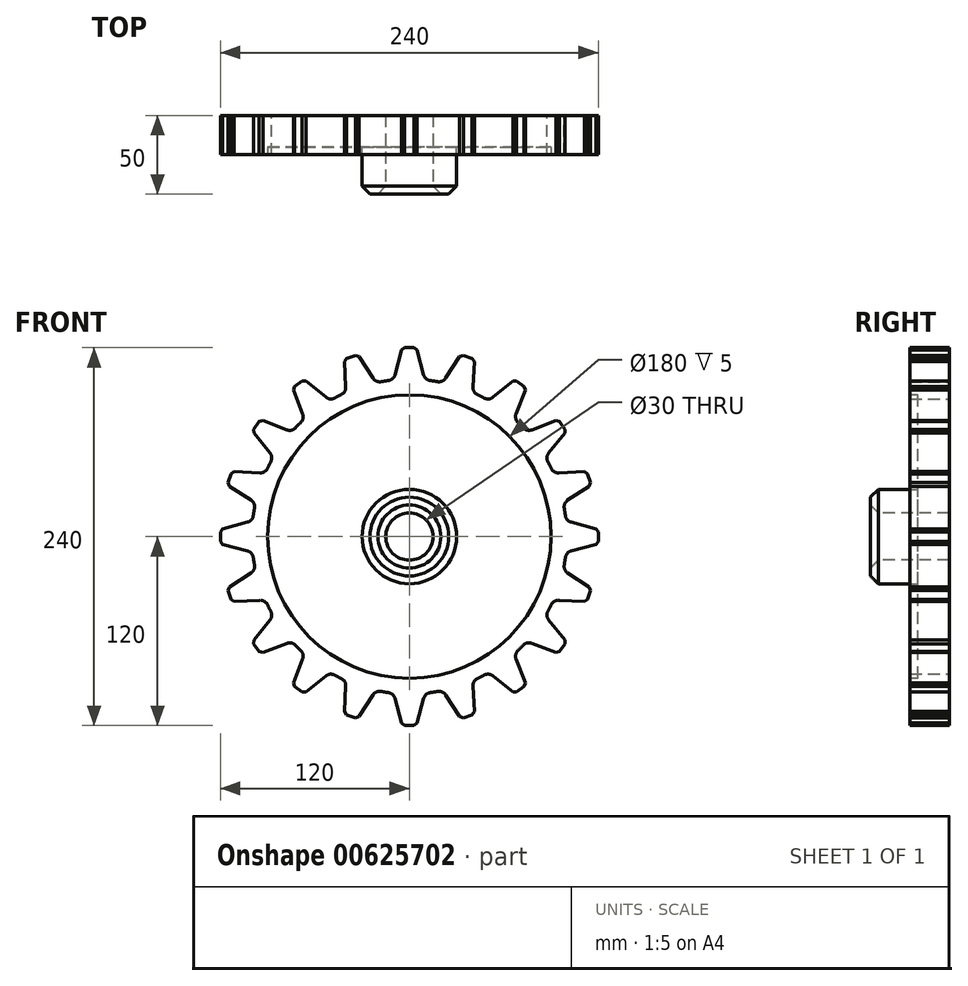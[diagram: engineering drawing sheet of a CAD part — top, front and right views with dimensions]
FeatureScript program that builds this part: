
annotation { "Feature Type Name" : "Feature", "Feature Type Description" : "" }
export const myFeature = defineFeature(function(context is Context, id is Id, definition is map)
    precondition{}
    {
        {
            var Q0;
            Q0=qCreatedBy(makeId("Front.planeOp"),FACE);
            var sketch = newSketch(context, id + "F0", { "sketchPlane" : qUnion([Q0])});
            skArc(sketch, "E0", {"start": v(21.24, 97.72) * mm, "mid": v(15.64, 98.77) * mm, "end": v(10, 99.5) * mm});
            skCircle(sketch, "E1", {"center": v(0, 0) * mm, "radius": 120 * mm, "construction": true});
            skLineSegment(sketch, "E2", {"start": v(0, 120) * mm, "end": v(-4.5, 120) * mm});
            skLineSegment(sketch, "E3", {"start": v(0, 120) * mm, "end": v(4.5, 120) * mm});
            skLineSegment(sketch, "E4", {"start": v(-4.5, 120) * mm, "end": v(-10, 99.5) * mm});
            skLineSegment(sketch, "E5", {"start": v(4.5, 120) * mm, "end": v(10, 99.5) * mm});
            skLineSegment(sketch, "E6.1.0", {"start": v(-41.36, 112.74) * mm, "end": v(-40.25, 91.54) * mm});
            skLineSegment(sketch, "E6.1.1", {"start": v(-37.08, 114.13) * mm, "end": v(-41.36, 112.74) * mm});
            skLineSegment(sketch, "E6.1.2", {"start": v(-37.08, 114.13) * mm, "end": v(-32.8, 115.52) * mm});
            skLineSegment(sketch, "E6.1.3", {"start": v(-32.8, 115.52) * mm, "end": v(-21.24, 97.72) * mm});
            skLineSegment(sketch, "E6.2.0", {"start": v(-74.17, 94.44) * mm, "end": v(-66.57, 74.62) * mm});
            skLineSegment(sketch, "E6.2.1", {"start": v(-70.53, 97.08) * mm, "end": v(-74.17, 94.44) * mm});
            skLineSegment(sketch, "E6.2.2", {"start": v(-70.53, 97.08) * mm, "end": v(-66.9, 99.73) * mm});
            skLineSegment(sketch, "E6.2.3", {"start": v(-66.9, 99.73) * mm, "end": v(-50.4, 86.37) * mm});
            skLineSegment(sketch, "E6.3.0", {"start": v(-99.73, 66.9) * mm, "end": v(-86.37, 50.4) * mm});
            skLineSegment(sketch, "E6.3.1", {"start": v(-97.08, 70.53) * mm, "end": v(-99.73, 66.9) * mm});
            skLineSegment(sketch, "E6.3.2", {"start": v(-97.08, 70.53) * mm, "end": v(-94.44, 74.17) * mm});
            skLineSegment(sketch, "E6.3.3", {"start": v(-94.44, 74.17) * mm, "end": v(-74.62, 66.57) * mm});
            skLineSegment(sketch, "E6.4.0", {"start": v(-115.52, 32.8) * mm, "end": v(-97.72, 21.24) * mm});
            skLineSegment(sketch, "E6.4.1", {"start": v(-114.13, 37.08) * mm, "end": v(-115.52, 32.8) * mm});
            skLineSegment(sketch, "E6.4.2", {"start": v(-114.13, 37.08) * mm, "end": v(-112.74, 41.36) * mm});
            skLineSegment(sketch, "E6.4.3", {"start": v(-112.74, 41.36) * mm, "end": v(-91.54, 40.25) * mm});
            skLineSegment(sketch, "E6.5.0", {"start": v(-120, -4.5) * mm, "end": v(-99.5, -10) * mm});
            skLineSegment(sketch, "E6.5.1", {"start": v(-120, 0) * mm, "end": v(-120, -4.5) * mm});
            skLineSegment(sketch, "E6.5.2", {"start": v(-120, 0) * mm, "end": v(-120, 4.5) * mm});
            skLineSegment(sketch, "E6.5.3", {"start": v(-120, 4.5) * mm, "end": v(-99.5, 10) * mm});
            skLineSegment(sketch, "E6.6.0", {"start": v(-112.74, -41.36) * mm, "end": v(-91.54, -40.25) * mm});
            skLineSegment(sketch, "E6.6.1", {"start": v(-114.13, -37.08) * mm, "end": v(-112.74, -41.36) * mm});
            skLineSegment(sketch, "E6.6.2", {"start": v(-114.13, -37.08) * mm, "end": v(-115.52, -32.8) * mm});
            skLineSegment(sketch, "E6.6.3", {"start": v(-115.52, -32.8) * mm, "end": v(-97.72, -21.24) * mm});
            skLineSegment(sketch, "E6.7.0", {"start": v(-94.44, -74.17) * mm, "end": v(-74.62, -66.57) * mm});
            skLineSegment(sketch, "E6.7.1", {"start": v(-97.08, -70.53) * mm, "end": v(-94.44, -74.17) * mm});
            skLineSegment(sketch, "E6.7.2", {"start": v(-97.08, -70.53) * mm, "end": v(-99.73, -66.9) * mm});
            skLineSegment(sketch, "E6.7.3", {"start": v(-99.73, -66.9) * mm, "end": v(-86.37, -50.4) * mm});
            skLineSegment(sketch, "E6.8.0", {"start": v(-66.9, -99.73) * mm, "end": v(-50.4, -86.37) * mm});
            skLineSegment(sketch, "E6.8.1", {"start": v(-70.53, -97.08) * mm, "end": v(-66.9, -99.73) * mm});
            skLineSegment(sketch, "E6.8.2", {"start": v(-70.53, -97.08) * mm, "end": v(-74.17, -94.44) * mm});
            skLineSegment(sketch, "E6.8.3", {"start": v(-74.17, -94.44) * mm, "end": v(-66.57, -74.62) * mm});
            skLineSegment(sketch, "E6.9.0", {"start": v(-32.8, -115.52) * mm, "end": v(-21.24, -97.72) * mm});
            skLineSegment(sketch, "E6.9.1", {"start": v(-37.08, -114.13) * mm, "end": v(-32.8, -115.52) * mm});
            skLineSegment(sketch, "E6.9.2", {"start": v(-37.08, -114.13) * mm, "end": v(-41.36, -112.74) * mm});
            skLineSegment(sketch, "E6.9.3", {"start": v(-41.36, -112.74) * mm, "end": v(-40.25, -91.54) * mm});
            skLineSegment(sketch, "E6.10.0", {"start": v(4.5, -120) * mm, "end": v(10, -99.5) * mm});
            skLineSegment(sketch, "E6.10.1", {"start": v(0, -120) * mm, "end": v(4.5, -120) * mm});
            skLineSegment(sketch, "E6.10.2", {"start": v(0, -120) * mm, "end": v(-4.5, -120) * mm});
            skLineSegment(sketch, "E6.10.3", {"start": v(-4.5, -120) * mm, "end": v(-10, -99.5) * mm});
            skLineSegment(sketch, "E6.11.0", {"start": v(41.36, -112.74) * mm, "end": v(40.25, -91.54) * mm});
            skLineSegment(sketch, "E6.11.1", {"start": v(37.08, -114.13) * mm, "end": v(41.36, -112.74) * mm});
            skLineSegment(sketch, "E6.11.2", {"start": v(37.08, -114.13) * mm, "end": v(32.8, -115.52) * mm});
            skLineSegment(sketch, "E6.11.3", {"start": v(32.8, -115.52) * mm, "end": v(21.24, -97.72) * mm});
            skLineSegment(sketch, "E6.12.0", {"start": v(74.17, -94.44) * mm, "end": v(66.57, -74.62) * mm});
            skLineSegment(sketch, "E6.12.1", {"start": v(70.53, -97.08) * mm, "end": v(74.17, -94.44) * mm});
            skLineSegment(sketch, "E6.12.2", {"start": v(70.53, -97.08) * mm, "end": v(66.9, -99.73) * mm});
            skLineSegment(sketch, "E6.12.3", {"start": v(66.9, -99.73) * mm, "end": v(50.4, -86.37) * mm});
            skLineSegment(sketch, "E6.13.0", {"start": v(99.73, -66.9) * mm, "end": v(86.37, -50.4) * mm});
            skLineSegment(sketch, "E6.13.1", {"start": v(97.08, -70.53) * mm, "end": v(99.73, -66.9) * mm});
            skLineSegment(sketch, "E6.13.2", {"start": v(97.08, -70.53) * mm, "end": v(94.44, -74.17) * mm});
            skLineSegment(sketch, "E6.13.3", {"start": v(94.44, -74.17) * mm, "end": v(74.62, -66.57) * mm});
            skLineSegment(sketch, "E6.14.0", {"start": v(115.52, -32.8) * mm, "end": v(97.72, -21.24) * mm});
            skLineSegment(sketch, "E6.14.1", {"start": v(114.13, -37.08) * mm, "end": v(115.52, -32.8) * mm});
            skLineSegment(sketch, "E6.14.2", {"start": v(114.13, -37.08) * mm, "end": v(112.74, -41.36) * mm});
            skLineSegment(sketch, "E6.14.3", {"start": v(112.74, -41.36) * mm, "end": v(91.54, -40.25) * mm});
            skLineSegment(sketch, "E6.15.0", {"start": v(120, 4.5) * mm, "end": v(99.5, 10) * mm});
            skLineSegment(sketch, "E6.15.1", {"start": v(120, 0) * mm, "end": v(120, 4.5) * mm});
            skLineSegment(sketch, "E6.15.2", {"start": v(120, 0) * mm, "end": v(120, -4.5) * mm});
            skLineSegment(sketch, "E6.15.3", {"start": v(120, -4.5) * mm, "end": v(99.5, -10) * mm});
            skLineSegment(sketch, "E6.16.0", {"start": v(112.74, 41.36) * mm, "end": v(91.54, 40.25) * mm});
            skLineSegment(sketch, "E6.16.1", {"start": v(114.13, 37.08) * mm, "end": v(112.74, 41.36) * mm});
            skLineSegment(sketch, "E6.16.2", {"start": v(114.13, 37.08) * mm, "end": v(115.52, 32.8) * mm});
            skLineSegment(sketch, "E6.16.3", {"start": v(115.52, 32.8) * mm, "end": v(97.72, 21.24) * mm});
            skLineSegment(sketch, "E6.17.0", {"start": v(94.44, 74.17) * mm, "end": v(74.62, 66.57) * mm});
            skLineSegment(sketch, "E6.17.1", {"start": v(97.08, 70.53) * mm, "end": v(94.44, 74.17) * mm});
            skLineSegment(sketch, "E6.17.2", {"start": v(97.08, 70.53) * mm, "end": v(99.73, 66.9) * mm});
            skLineSegment(sketch, "E6.17.3", {"start": v(99.73, 66.9) * mm, "end": v(86.37, 50.4) * mm});
            skLineSegment(sketch, "E6.18.0", {"start": v(66.9, 99.73) * mm, "end": v(50.4, 86.37) * mm});
            skLineSegment(sketch, "E6.18.1", {"start": v(70.53, 97.08) * mm, "end": v(66.9, 99.73) * mm});
            skLineSegment(sketch, "E6.18.2", {"start": v(70.53, 97.08) * mm, "end": v(74.17, 94.44) * mm});
            skLineSegment(sketch, "E6.18.3", {"start": v(74.17, 94.44) * mm, "end": v(66.57, 74.62) * mm});
            skLineSegment(sketch, "E6.19.0", {"start": v(32.8, 115.52) * mm, "end": v(21.24, 97.72) * mm});
            skLineSegment(sketch, "E6.19.1", {"start": v(37.08, 114.13) * mm, "end": v(32.8, 115.52) * mm});
            skLineSegment(sketch, "E6.19.2", {"start": v(37.08, 114.13) * mm, "end": v(41.36, 112.74) * mm});
            skLineSegment(sketch, "E6.19.3", {"start": v(41.36, 112.74) * mm, "end": v(40.25, 91.54) * mm});
            skArc(sketch, "E7.trimOffspring", {"start": v(-40.25, 91.54) * mm, "mid": v(-45.4, 89.1) * mm, "end": v(-50.4, 86.37) * mm});
            skArc(sketch, "E8.trimOffspring", {"start": v(-66.57, 74.62) * mm, "mid": v(-70.71, 70.71) * mm, "end": v(-74.62, 66.57) * mm});
            skArc(sketch, "E9.trimOffspring", {"start": v(-86.37, 50.4) * mm, "mid": v(-89.1, 45.4) * mm, "end": v(-91.54, 40.25) * mm});
            skArc(sketch, "E10.trimOffspring", {"start": v(-97.72, 21.24) * mm, "mid": v(-98.77, 15.64) * mm, "end": v(-99.5, 10) * mm});
            skArc(sketch, "E11.trimOffspring", {"start": v(-99.5, -10) * mm, "mid": v(-98.77, -15.64) * mm, "end": v(-97.72, -21.24) * mm});
            skArc(sketch, "E12.trimOffspring", {"start": v(-91.54, -40.25) * mm, "mid": v(-89.1, -45.4) * mm, "end": v(-86.37, -50.4) * mm});
            skArc(sketch, "E13.trimOffspring", {"start": v(-74.62, -66.57) * mm, "mid": v(-70.71, -70.71) * mm, "end": v(-66.57, -74.62) * mm});
            skArc(sketch, "E14.trimOffspring", {"start": v(-50.4, -86.37) * mm, "mid": v(-45.4, -89.1) * mm, "end": v(-40.25, -91.54) * mm});
            skArc(sketch, "E15.trimOffspring", {"start": v(-21.24, -97.72) * mm, "mid": v(-15.64, -98.77) * mm, "end": v(-10, -99.5) * mm});
            skArc(sketch, "E16.trimOffspring", {"start": v(10, -99.5) * mm, "mid": v(15.64, -98.77) * mm, "end": v(21.24, -97.72) * mm});
            skArc(sketch, "E17.trimOffspring", {"start": v(40.25, -91.54) * mm, "mid": v(45.4, -89.1) * mm, "end": v(50.4, -86.37) * mm});
            skArc(sketch, "E18.trimOffspring", {"start": v(66.57, -74.62) * mm, "mid": v(70.71, -70.71) * mm, "end": v(74.62, -66.57) * mm});
            skArc(sketch, "E19.trimOffspring", {"start": v(86.37, -50.4) * mm, "mid": v(89.1, -45.4) * mm, "end": v(91.54, -40.25) * mm});
            skArc(sketch, "E20.trimOffspring", {"start": v(97.72, -21.24) * mm, "mid": v(98.77, -15.64) * mm, "end": v(99.5, -10) * mm});
            skArc(sketch, "E21.trimOffspring", {"start": v(99.5, 10) * mm, "mid": v(98.77, 15.64) * mm, "end": v(97.72, 21.24) * mm});
            skArc(sketch, "E22.trimOffspring", {"start": v(91.54, 40.25) * mm, "mid": v(89.1, 45.4) * mm, "end": v(86.37, 50.4) * mm});
            skArc(sketch, "E23.trimOffspring", {"start": v(74.62, 66.57) * mm, "mid": v(70.71, 70.71) * mm, "end": v(66.57, 74.62) * mm});
            skArc(sketch, "E24.trimOffspring", {"start": v(50.4, 86.37) * mm, "mid": v(45.4, 89.1) * mm, "end": v(40.25, 91.54) * mm});
            skArc(sketch, "E25.trimOffspring", {"start": v(-10, 99.5) * mm, "mid": v(-15.64, 98.77) * mm, "end": v(-21.24, 97.72) * mm});
            skSolve(sketch);
        }
        {
            var Q0;
            Q0=makeQuery(id+"F0.imprint","IMPRINT",FACE,{"disambiguationData":[TD([[makeQuery(id+"F0.imprint","IMPRINT",EDGE,{"derivedFrom":sQuery(id+"F0.wireOp",EDGE,"E0")}),1.0]])]});
            extrude(context, id + "F1", {"entities" : qUnion([Q0]), "depth" : 25 * mm, "offsetDistance" : 25 * mm});
        }
        {
            var Q0;
            Q0=makeQuery(id+"F1.opExtrude","SWEPT_EDGE",EDGE,{"disambiguationData":[OSD([sQuery(id+"F0.wireOp",EDGE,"E0"),sQuery(id+"F0.wireOp",EDGE,"E5")])]});
            var Q1;
            Q1=makeQuery(id+"F1.opExtrude","SWEPT_EDGE",EDGE,{"disambiguationData":[OSD([sQuery(id+"F0.wireOp",EDGE,"E0"),sQuery(id+"F0.wireOp",EDGE,"E6.19.0")])]});
            var Q2;
            Q2=makeQuery(id+"F1.opExtrude","SWEPT_EDGE",EDGE,{"disambiguationData":[OSD([sQuery(id+"F0.wireOp",EDGE,"E6.1.3"),sQuery(id+"F0.wireOp",EDGE,"E25.trimOffspring")])]});
            var Q3;
            Q3=makeQuery(id+"F1.opExtrude","SWEPT_EDGE",EDGE,{"disambiguationData":[OSD([sQuery(id+"F0.wireOp",EDGE,"E4"),sQuery(id+"F0.wireOp",EDGE,"E25.trimOffspring")])]});
            var Q4;
            Q4=makeQuery(id+"F1.opExtrude","SWEPT_EDGE",EDGE,{"disambiguationData":[OSD([sQuery(id+"F0.wireOp",EDGE,"E6.2.3"),sQuery(id+"F0.wireOp",EDGE,"E7.trimOffspring")])]});
            var Q5;
            Q5=makeQuery(id+"F1.opExtrude","SWEPT_EDGE",EDGE,{"disambiguationData":[OSD([sQuery(id+"F0.wireOp",EDGE,"E6.3.3"),sQuery(id+"F0.wireOp",EDGE,"E8.trimOffspring")])]});
            var Q6;
            Q6=makeQuery(id+"F1.opExtrude","SWEPT_EDGE",EDGE,{"disambiguationData":[OSD([sQuery(id+"F0.wireOp",EDGE,"E6.2.0"),sQuery(id+"F0.wireOp",EDGE,"E8.trimOffspring")])]});
            var Q7;
            Q7=makeQuery(id+"F1.opExtrude","SWEPT_EDGE",EDGE,{"disambiguationData":[OSD([sQuery(id+"F0.wireOp",EDGE,"E6.1.0"),sQuery(id+"F0.wireOp",EDGE,"E7.trimOffspring")])]});
            var Q8;
            Q8=makeQuery(id+"F1.opExtrude","SWEPT_EDGE",EDGE,{"disambiguationData":[OSD([sQuery(id+"F0.wireOp",EDGE,"E6.4.3"),sQuery(id+"F0.wireOp",EDGE,"E9.trimOffspring")])]});
            var Q9;
            Q9=makeQuery(id+"F1.opExtrude","SWEPT_EDGE",EDGE,{"disambiguationData":[OSD([sQuery(id+"F0.wireOp",EDGE,"E6.3.0"),sQuery(id+"F0.wireOp",EDGE,"E9.trimOffspring")])]});
            var Q10;
            Q10=makeQuery(id+"F1.opExtrude","SWEPT_EDGE",EDGE,{"disambiguationData":[OSD([sQuery(id+"F0.wireOp",EDGE,"E6.5.3"),sQuery(id+"F0.wireOp",EDGE,"E10.trimOffspring")])]});
            var Q11;
            Q11=makeQuery(id+"F1.opExtrude","SWEPT_EDGE",EDGE,{"disambiguationData":[OSD([sQuery(id+"F0.wireOp",EDGE,"E6.4.0"),sQuery(id+"F0.wireOp",EDGE,"E10.trimOffspring")])]});
            var Q12;
            Q12=makeQuery(id+"F1.opExtrude","SWEPT_EDGE",EDGE,{"disambiguationData":[OSD([sQuery(id+"F0.wireOp",EDGE,"E6.5.0"),sQuery(id+"F0.wireOp",EDGE,"E11.trimOffspring")])]});
            var Q13;
            Q13=makeQuery(id+"F1.opExtrude","SWEPT_EDGE",EDGE,{"disambiguationData":[OSD([sQuery(id+"F0.wireOp",EDGE,"E6.6.3"),sQuery(id+"F0.wireOp",EDGE,"E11.trimOffspring")])]});
            var Q14;
            Q14=makeQuery(id+"F1.opExtrude","SWEPT_EDGE",EDGE,{"disambiguationData":[OSD([sQuery(id+"F0.wireOp",EDGE,"E6.7.3"),sQuery(id+"F0.wireOp",EDGE,"E12.trimOffspring")])]});
            var Q15;
            Q15=makeQuery(id+"F1.opExtrude","SWEPT_EDGE",EDGE,{"disambiguationData":[OSD([sQuery(id+"F0.wireOp",EDGE,"E6.6.0"),sQuery(id+"F0.wireOp",EDGE,"E12.trimOffspring")])]});
            var Q16;
            Q16=makeQuery(id+"F1.opExtrude","SWEPT_EDGE",EDGE,{"disambiguationData":[OSD([sQuery(id+"F0.wireOp",EDGE,"E6.7.0"),sQuery(id+"F0.wireOp",EDGE,"E13.trimOffspring")])]});
            var Q17;
            Q17=makeQuery(id+"F1.opExtrude","SWEPT_EDGE",EDGE,{"disambiguationData":[OSD([sQuery(id+"F0.wireOp",EDGE,"E6.8.3"),sQuery(id+"F0.wireOp",EDGE,"E13.trimOffspring")])]});
            var Q18;
            Q18=makeQuery(id+"F1.opExtrude","SWEPT_EDGE",EDGE,{"disambiguationData":[OSD([sQuery(id+"F0.wireOp",EDGE,"E6.9.3"),sQuery(id+"F0.wireOp",EDGE,"E14.trimOffspring")])]});
            var Q19;
            Q19=makeQuery(id+"F1.opExtrude","SWEPT_EDGE",EDGE,{"disambiguationData":[OSD([sQuery(id+"F0.wireOp",EDGE,"E6.8.0"),sQuery(id+"F0.wireOp",EDGE,"E14.trimOffspring")])]});
            var Q20;
            Q20=makeQuery(id+"F1.opExtrude","SWEPT_EDGE",EDGE,{"disambiguationData":[OSD([sQuery(id+"F0.wireOp",EDGE,"E6.9.0"),sQuery(id+"F0.wireOp",EDGE,"E15.trimOffspring")])]});
            var Q21;
            Q21=makeQuery(id+"F1.opExtrude","SWEPT_EDGE",EDGE,{"disambiguationData":[OSD([sQuery(id+"F0.wireOp",EDGE,"E6.10.3"),sQuery(id+"F0.wireOp",EDGE,"E15.trimOffspring")])]});
            var Q22;
            Q22=makeQuery(id+"F1.opExtrude","SWEPT_EDGE",EDGE,{"disambiguationData":[OSD([sQuery(id+"F0.wireOp",EDGE,"E6.10.0"),sQuery(id+"F0.wireOp",EDGE,"E16.trimOffspring")])]});
            var Q23;
            Q23=makeQuery(id+"F1.opExtrude","SWEPT_EDGE",EDGE,{"disambiguationData":[OSD([sQuery(id+"F0.wireOp",EDGE,"E6.11.3"),sQuery(id+"F0.wireOp",EDGE,"E16.trimOffspring")])]});
            var Q24;
            Q24=makeQuery(id+"F1.opExtrude","SWEPT_EDGE",EDGE,{"disambiguationData":[OSD([sQuery(id+"F0.wireOp",EDGE,"E6.11.0"),sQuery(id+"F0.wireOp",EDGE,"E17.trimOffspring")])]});
            var Q25;
            Q25=makeQuery(id+"F1.opExtrude","SWEPT_EDGE",EDGE,{"disambiguationData":[OSD([sQuery(id+"F0.wireOp",EDGE,"E6.12.3"),sQuery(id+"F0.wireOp",EDGE,"E17.trimOffspring")])]});
            var Q26;
            Q26=makeQuery(id+"F1.opExtrude","SWEPT_EDGE",EDGE,{"disambiguationData":[OSD([sQuery(id+"F0.wireOp",EDGE,"E6.12.0"),sQuery(id+"F0.wireOp",EDGE,"E18.trimOffspring")])]});
            var Q27;
            Q27=makeQuery(id+"F1.opExtrude","SWEPT_EDGE",EDGE,{"disambiguationData":[OSD([sQuery(id+"F0.wireOp",EDGE,"E6.13.3"),sQuery(id+"F0.wireOp",EDGE,"E18.trimOffspring")])]});
            var Q28;
            Q28=makeQuery(id+"F1.opExtrude","SWEPT_EDGE",EDGE,{"disambiguationData":[OSD([sQuery(id+"F0.wireOp",EDGE,"E6.14.3"),sQuery(id+"F0.wireOp",EDGE,"E19.trimOffspring")])]});
            var Q29;
            Q29=makeQuery(id+"F1.opExtrude","SWEPT_EDGE",EDGE,{"disambiguationData":[OSD([sQuery(id+"F0.wireOp",EDGE,"E6.13.0"),sQuery(id+"F0.wireOp",EDGE,"E19.trimOffspring")])]});
            var Q30;
            Q30=makeQuery(id+"F1.opExtrude","SWEPT_EDGE",EDGE,{"disambiguationData":[OSD([sQuery(id+"F0.wireOp",EDGE,"E6.15.3"),sQuery(id+"F0.wireOp",EDGE,"E20.trimOffspring")])]});
            var Q31;
            Q31=makeQuery(id+"F1.opExtrude","SWEPT_EDGE",EDGE,{"disambiguationData":[OSD([sQuery(id+"F0.wireOp",EDGE,"E6.14.0"),sQuery(id+"F0.wireOp",EDGE,"E20.trimOffspring")])]});
            var Q32;
            Q32=makeQuery(id+"F1.opExtrude","SWEPT_EDGE",EDGE,{"disambiguationData":[OSD([sQuery(id+"F0.wireOp",EDGE,"E6.16.3"),sQuery(id+"F0.wireOp",EDGE,"E21.trimOffspring")])]});
            var Q33;
            Q33=makeQuery(id+"F1.opExtrude","SWEPT_EDGE",EDGE,{"disambiguationData":[OSD([sQuery(id+"F0.wireOp",EDGE,"E6.15.0"),sQuery(id+"F0.wireOp",EDGE,"E21.trimOffspring")])]});
            var Q34;
            Q34=makeQuery(id+"F1.opExtrude","SWEPT_EDGE",EDGE,{"disambiguationData":[OSD([sQuery(id+"F0.wireOp",EDGE,"E6.17.3"),sQuery(id+"F0.wireOp",EDGE,"E22.trimOffspring")])]});
            var Q35;
            Q35=makeQuery(id+"F1.opExtrude","SWEPT_EDGE",EDGE,{"disambiguationData":[OSD([sQuery(id+"F0.wireOp",EDGE,"E6.16.0"),sQuery(id+"F0.wireOp",EDGE,"E22.trimOffspring")])]});
            var Q36;
            Q36=makeQuery(id+"F1.opExtrude","SWEPT_EDGE",EDGE,{"disambiguationData":[OSD([sQuery(id+"F0.wireOp",EDGE,"E6.18.3"),sQuery(id+"F0.wireOp",EDGE,"E23.trimOffspring")])]});
            var Q37;
            Q37=makeQuery(id+"F1.opExtrude","SWEPT_EDGE",EDGE,{"disambiguationData":[OSD([sQuery(id+"F0.wireOp",EDGE,"E6.17.0"),sQuery(id+"F0.wireOp",EDGE,"E23.trimOffspring")])]});
            var Q38;
            Q38=makeQuery(id+"F1.opExtrude","SWEPT_EDGE",EDGE,{"disambiguationData":[OSD([sQuery(id+"F0.wireOp",EDGE,"E6.18.0"),sQuery(id+"F0.wireOp",EDGE,"E24.trimOffspring")])]});
            var Q39;
            Q39=makeQuery(id+"F1.opExtrude","SWEPT_EDGE",EDGE,{"disambiguationData":[OSD([sQuery(id+"F0.wireOp",EDGE,"E6.19.3"),sQuery(id+"F0.wireOp",EDGE,"E24.trimOffspring")])]});
            fillet(context, id + "F2", {"entities" : qUnion([Q0, Q1, Q2, Q3, Q4, Q5, Q6, Q7, Q8, Q9, Q10, Q11, Q12, Q13, Q14, Q15, Q16, Q17, Q18, Q19, Q20, Q21, Q22, Q23, Q24, Q25, Q26, Q27, Q28, Q29, Q30, Q31, Q32, Q33, Q34, Q35, Q36, Q37, Q38, Q39]), "radius" : 5 * mm, "tangentPropagation" : true, "allowEdgeOverflow" : false});
        }
        {
            var Q0;
            Q0=makeQuery(id+"F1.opExtrude","SWEPT_EDGE",EDGE,{"disambiguationData":[OSD([sQuery(id+"F0.wireOp",EDGE,"E3"),sQuery(id+"F0.wireOp",EDGE,"E5")])]});
            var Q1;
            Q1=makeQuery(id+"F1.opExtrude","SWEPT_EDGE",EDGE,{"disambiguationData":[OSD([sQuery(id+"F0.wireOp",EDGE,"E2"),sQuery(id+"F0.wireOp",EDGE,"E4")])]});
            var Q2;
            Q2=makeQuery(id+"F1.opExtrude","SWEPT_EDGE",EDGE,{"disambiguationData":[OSD([sQuery(id+"F0.wireOp",EDGE,"E6.1.2"),sQuery(id+"F0.wireOp",EDGE,"E6.1.3")])]});
            var Q3;
            Q3=makeQuery(id+"F1.opExtrude","SWEPT_EDGE",EDGE,{"disambiguationData":[OSD([sQuery(id+"F0.wireOp",EDGE,"E6.1.0"),sQuery(id+"F0.wireOp",EDGE,"E6.1.1")])]});
            var Q4;
            Q4=makeQuery(id+"F1.opExtrude","SWEPT_EDGE",EDGE,{"disambiguationData":[OSD([sQuery(id+"F0.wireOp",EDGE,"E6.2.2"),sQuery(id+"F0.wireOp",EDGE,"E6.2.3")])]});
            var Q5;
            Q5=makeQuery(id+"F1.opExtrude","SWEPT_EDGE",EDGE,{"disambiguationData":[OSD([sQuery(id+"F0.wireOp",EDGE,"E6.2.0"),sQuery(id+"F0.wireOp",EDGE,"E6.2.1")])]});
            var Q6;
            Q6=makeQuery(id+"F1.opExtrude","SWEPT_EDGE",EDGE,{"disambiguationData":[OSD([sQuery(id+"F0.wireOp",EDGE,"E6.3.2"),sQuery(id+"F0.wireOp",EDGE,"E6.3.3")])]});
            var Q7;
            Q7=makeQuery(id+"F1.opExtrude","SWEPT_EDGE",EDGE,{"disambiguationData":[OSD([sQuery(id+"F0.wireOp",EDGE,"E6.3.0"),sQuery(id+"F0.wireOp",EDGE,"E6.3.1")])]});
            var Q8;
            Q8=makeQuery(id+"F1.opExtrude","SWEPT_EDGE",EDGE,{"disambiguationData":[OSD([sQuery(id+"F0.wireOp",EDGE,"E6.4.2"),sQuery(id+"F0.wireOp",EDGE,"E6.4.3")])]});
            var Q9;
            Q9=makeQuery(id+"F1.opExtrude","SWEPT_EDGE",EDGE,{"disambiguationData":[OSD([sQuery(id+"F0.wireOp",EDGE,"E6.4.0"),sQuery(id+"F0.wireOp",EDGE,"E6.4.1")])]});
            var Q10;
            Q10=makeQuery(id+"F1.opExtrude","SWEPT_EDGE",EDGE,{"disambiguationData":[OSD([sQuery(id+"F0.wireOp",EDGE,"E6.5.2"),sQuery(id+"F0.wireOp",EDGE,"E6.5.3")])]});
            var Q11;
            Q11=makeQuery(id+"F1.opExtrude","SWEPT_EDGE",EDGE,{"disambiguationData":[OSD([sQuery(id+"F0.wireOp",EDGE,"E6.5.0"),sQuery(id+"F0.wireOp",EDGE,"E6.5.1")])]});
            var Q12;
            Q12=makeQuery(id+"F1.opExtrude","SWEPT_EDGE",EDGE,{"disambiguationData":[OSD([sQuery(id+"F0.wireOp",EDGE,"E6.6.2"),sQuery(id+"F0.wireOp",EDGE,"E6.6.3")])]});
            var Q13;
            Q13=makeQuery(id+"F1.opExtrude","SWEPT_EDGE",EDGE,{"disambiguationData":[OSD([sQuery(id+"F0.wireOp",EDGE,"E6.6.0"),sQuery(id+"F0.wireOp",EDGE,"E6.6.1")])]});
            var Q14;
            Q14=makeQuery(id+"F1.opExtrude","SWEPT_EDGE",EDGE,{"disambiguationData":[OSD([sQuery(id+"F0.wireOp",EDGE,"E6.7.2"),sQuery(id+"F0.wireOp",EDGE,"E6.7.3")])]});
            var Q15;
            Q15=makeQuery(id+"F1.opExtrude","SWEPT_EDGE",EDGE,{"disambiguationData":[OSD([sQuery(id+"F0.wireOp",EDGE,"E6.7.0"),sQuery(id+"F0.wireOp",EDGE,"E6.7.1")])]});
            var Q16;
            Q16=makeQuery(id+"F1.opExtrude","SWEPT_EDGE",EDGE,{"disambiguationData":[OSD([sQuery(id+"F0.wireOp",EDGE,"E6.8.2"),sQuery(id+"F0.wireOp",EDGE,"E6.8.3")])]});
            var Q17;
            Q17=makeQuery(id+"F1.opExtrude","SWEPT_EDGE",EDGE,{"disambiguationData":[OSD([sQuery(id+"F0.wireOp",EDGE,"E6.8.0"),sQuery(id+"F0.wireOp",EDGE,"E6.8.1")])]});
            var Q18;
            Q18=makeQuery(id+"F1.opExtrude","SWEPT_EDGE",EDGE,{"disambiguationData":[OSD([sQuery(id+"F0.wireOp",EDGE,"E6.9.2"),sQuery(id+"F0.wireOp",EDGE,"E6.9.3")])]});
            var Q19;
            Q19=makeQuery(id+"F1.opExtrude","SWEPT_EDGE",EDGE,{"disambiguationData":[OSD([sQuery(id+"F0.wireOp",EDGE,"E6.9.0"),sQuery(id+"F0.wireOp",EDGE,"E6.9.1")])]});
            var Q20;
            Q20=makeQuery(id+"F1.opExtrude","SWEPT_EDGE",EDGE,{"disambiguationData":[OSD([sQuery(id+"F0.wireOp",EDGE,"E6.10.2"),sQuery(id+"F0.wireOp",EDGE,"E6.10.3")])]});
            var Q21;
            Q21=makeQuery(id+"F1.opExtrude","SWEPT_EDGE",EDGE,{"disambiguationData":[OSD([sQuery(id+"F0.wireOp",EDGE,"E6.10.0"),sQuery(id+"F0.wireOp",EDGE,"E6.10.1")])]});
            var Q22;
            Q22=makeQuery(id+"F1.opExtrude","SWEPT_EDGE",EDGE,{"disambiguationData":[OSD([sQuery(id+"F0.wireOp",EDGE,"E6.11.2"),sQuery(id+"F0.wireOp",EDGE,"E6.11.3")])]});
            var Q23;
            Q23=makeQuery(id+"F1.opExtrude","SWEPT_EDGE",EDGE,{"disambiguationData":[OSD([sQuery(id+"F0.wireOp",EDGE,"E6.11.0"),sQuery(id+"F0.wireOp",EDGE,"E6.11.1")])]});
            var Q24;
            Q24=makeQuery(id+"F1.opExtrude","SWEPT_EDGE",EDGE,{"disambiguationData":[OSD([sQuery(id+"F0.wireOp",EDGE,"E6.12.2"),sQuery(id+"F0.wireOp",EDGE,"E6.12.3")])]});
            var Q25;
            Q25=makeQuery(id+"F1.opExtrude","SWEPT_EDGE",EDGE,{"disambiguationData":[OSD([sQuery(id+"F0.wireOp",EDGE,"E6.12.0"),sQuery(id+"F0.wireOp",EDGE,"E6.12.1")])]});
            var Q26;
            Q26=makeQuery(id+"F1.opExtrude","SWEPT_EDGE",EDGE,{"disambiguationData":[OSD([sQuery(id+"F0.wireOp",EDGE,"E6.13.2"),sQuery(id+"F0.wireOp",EDGE,"E6.13.3")])]});
            var Q27;
            Q27=makeQuery(id+"F1.opExtrude","SWEPT_EDGE",EDGE,{"disambiguationData":[OSD([sQuery(id+"F0.wireOp",EDGE,"E6.13.0"),sQuery(id+"F0.wireOp",EDGE,"E6.13.1")])]});
            var Q28;
            Q28=makeQuery(id+"F1.opExtrude","SWEPT_EDGE",EDGE,{"disambiguationData":[OSD([sQuery(id+"F0.wireOp",EDGE,"E6.14.2"),sQuery(id+"F0.wireOp",EDGE,"E6.14.3")])]});
            var Q29;
            Q29=makeQuery(id+"F1.opExtrude","SWEPT_EDGE",EDGE,{"disambiguationData":[OSD([sQuery(id+"F0.wireOp",EDGE,"E6.14.0"),sQuery(id+"F0.wireOp",EDGE,"E6.14.1")])]});
            var Q30;
            Q30=makeQuery(id+"F1.opExtrude","SWEPT_EDGE",EDGE,{"disambiguationData":[OSD([sQuery(id+"F0.wireOp",EDGE,"E6.15.2"),sQuery(id+"F0.wireOp",EDGE,"E6.15.3")])]});
            var Q31;
            Q31=makeQuery(id+"F1.opExtrude","SWEPT_EDGE",EDGE,{"disambiguationData":[OSD([sQuery(id+"F0.wireOp",EDGE,"E6.15.0"),sQuery(id+"F0.wireOp",EDGE,"E6.15.1")])]});
            var Q32;
            Q32=makeQuery(id+"F1.opExtrude","SWEPT_EDGE",EDGE,{"disambiguationData":[OSD([sQuery(id+"F0.wireOp",EDGE,"E6.16.2"),sQuery(id+"F0.wireOp",EDGE,"E6.16.3")])]});
            var Q33;
            Q33=makeQuery(id+"F1.opExtrude","SWEPT_EDGE",EDGE,{"disambiguationData":[OSD([sQuery(id+"F0.wireOp",EDGE,"E6.16.0"),sQuery(id+"F0.wireOp",EDGE,"E6.16.1")])]});
            var Q34;
            Q34=makeQuery(id+"F1.opExtrude","SWEPT_EDGE",EDGE,{"disambiguationData":[OSD([sQuery(id+"F0.wireOp",EDGE,"E6.17.2"),sQuery(id+"F0.wireOp",EDGE,"E6.17.3")])]});
            var Q35;
            Q35=makeQuery(id+"F1.opExtrude","SWEPT_EDGE",EDGE,{"disambiguationData":[OSD([sQuery(id+"F0.wireOp",EDGE,"E6.17.0"),sQuery(id+"F0.wireOp",EDGE,"E6.17.1")])]});
            var Q36;
            Q36=makeQuery(id+"F1.opExtrude","SWEPT_EDGE",EDGE,{"disambiguationData":[OSD([sQuery(id+"F0.wireOp",EDGE,"E6.18.2"),sQuery(id+"F0.wireOp",EDGE,"E6.18.3")])]});
            var Q37;
            Q37=makeQuery(id+"F1.opExtrude","SWEPT_EDGE",EDGE,{"disambiguationData":[OSD([sQuery(id+"F0.wireOp",EDGE,"E6.18.0"),sQuery(id+"F0.wireOp",EDGE,"E6.18.1")])]});
            var Q38;
            Q38=makeQuery(id+"F1.opExtrude","SWEPT_EDGE",EDGE,{"disambiguationData":[OSD([sQuery(id+"F0.wireOp",EDGE,"E6.19.2"),sQuery(id+"F0.wireOp",EDGE,"E6.19.3")])]});
            var Q39;
            Q39=makeQuery(id+"F1.opExtrude","SWEPT_EDGE",EDGE,{"disambiguationData":[OSD([sQuery(id+"F0.wireOp",EDGE,"E6.19.0"),sQuery(id+"F0.wireOp",EDGE,"E6.19.1")])]});
            chamfer(context, id + "F3", {"entities" : qUnion([Q0, Q1, Q2, Q3, Q4, Q5, Q6, Q7, Q8, Q9, Q10, Q11, Q12, Q13, Q14, Q15, Q16, Q17, Q18, Q19, Q20, Q21, Q22, Q23, Q24, Q25, Q26, Q27, Q28, Q29, Q30, Q31, Q32, Q33, Q34, Q35, Q36, Q37, Q38, Q39]), "width" : 2 * mm, "tangentPropagation" : true});
        }
        {
            var Q0;
            Q0=makeQuery(id+"F1.opExtrude","CAP_FACE",FACE,{"disambiguationData":[OSD([sQuery(id+"F0.wireOp",EDGE,"E0"),sQuery(id+"F0.wireOp",EDGE,"E2"),sQuery(id+"F0.wireOp",EDGE,"E3"),sQuery(id+"F0.wireOp",EDGE,"E4"),sQuery(id+"F0.wireOp",EDGE,"E5"),sQuery(id+"F0.wireOp",EDGE,"E6.1.0"),sQuery(id+"F0.wireOp",EDGE,"E6.1.1"),sQuery(id+"F0.wireOp",EDGE,"E6.1.2"),sQuery(id+"F0.wireOp",EDGE,"E6.1.3"),sQuery(id+"F0.wireOp",EDGE,"E6.2.0"),sQuery(id+"F0.wireOp",EDGE,"E6.2.1"),sQuery(id+"F0.wireOp",EDGE,"E6.2.2"),sQuery(id+"F0.wireOp",EDGE,"E6.2.3"),sQuery(id+"F0.wireOp",EDGE,"E6.3.0"),sQuery(id+"F0.wireOp",EDGE,"E6.3.1"),sQuery(id+"F0.wireOp",EDGE,"E6.3.2"),sQuery(id+"F0.wireOp",EDGE,"E6.3.3"),sQuery(id+"F0.wireOp",EDGE,"E6.4.0"),sQuery(id+"F0.wireOp",EDGE,"E6.4.1"),sQuery(id+"F0.wireOp",EDGE,"E6.4.2"),sQuery(id+"F0.wireOp",EDGE,"E6.4.3"),sQuery(id+"F0.wireOp",EDGE,"E6.5.0"),sQuery(id+"F0.wireOp",EDGE,"E6.5.1"),sQuery(id+"F0.wireOp",EDGE,"E6.5.2"),sQuery(id+"F0.wireOp",EDGE,"E6.5.3"),sQuery(id+"F0.wireOp",EDGE,"E6.6.0"),sQuery(id+"F0.wireOp",EDGE,"E6.6.1"),sQuery(id+"F0.wireOp",EDGE,"E6.6.2"),sQuery(id+"F0.wireOp",EDGE,"E6.6.3"),sQuery(id+"F0.wireOp",EDGE,"E6.7.0"),sQuery(id+"F0.wireOp",EDGE,"E6.7.1"),sQuery(id+"F0.wireOp",EDGE,"E6.7.2"),sQuery(id+"F0.wireOp",EDGE,"E6.7.3"),sQuery(id+"F0.wireOp",EDGE,"E6.8.0"),sQuery(id+"F0.wireOp",EDGE,"E6.8.1"),sQuery(id+"F0.wireOp",EDGE,"E6.8.2"),sQuery(id+"F0.wireOp",EDGE,"E6.8.3"),sQuery(id+"F0.wireOp",EDGE,"E6.9.0"),sQuery(id+"F0.wireOp",EDGE,"E6.9.1"),sQuery(id+"F0.wireOp",EDGE,"E6.9.2"),sQuery(id+"F0.wireOp",EDGE,"E6.9.3"),sQuery(id+"F0.wireOp",EDGE,"E6.10.0"),sQuery(id+"F0.wireOp",EDGE,"E6.10.1"),sQuery(id+"F0.wireOp",EDGE,"E6.10.2"),sQuery(id+"F0.wireOp",EDGE,"E6.10.3"),sQuery(id+"F0.wireOp",EDGE,"E6.11.0"),sQuery(id+"F0.wireOp",EDGE,"E6.11.1"),sQuery(id+"F0.wireOp",EDGE,"E6.11.2"),sQuery(id+"F0.wireOp",EDGE,"E6.11.3"),sQuery(id+"F0.wireOp",EDGE,"E6.12.0"),sQuery(id+"F0.wireOp",EDGE,"E6.12.1"),sQuery(id+"F0.wireOp",EDGE,"E6.12.2"),sQuery(id+"F0.wireOp",EDGE,"E6.12.3"),sQuery(id+"F0.wireOp",EDGE,"E6.13.0"),sQuery(id+"F0.wireOp",EDGE,"E6.13.1"),sQuery(id+"F0.wireOp",EDGE,"E6.13.2"),sQuery(id+"F0.wireOp",EDGE,"E6.13.3"),sQuery(id+"F0.wireOp",EDGE,"E6.14.0"),sQuery(id+"F0.wireOp",EDGE,"E6.14.1"),sQuery(id+"F0.wireOp",EDGE,"E6.14.2"),sQuery(id+"F0.wireOp",EDGE,"E6.14.3"),sQuery(id+"F0.wireOp",EDGE,"E6.15.0"),sQuery(id+"F0.wireOp",EDGE,"E6.15.1"),sQuery(id+"F0.wireOp",EDGE,"E6.15.2"),sQuery(id+"F0.wireOp",EDGE,"E6.15.3"),sQuery(id+"F0.wireOp",EDGE,"E6.16.0"),sQuery(id+"F0.wireOp",EDGE,"E6.16.1"),sQuery(id+"F0.wireOp",EDGE,"E6.16.2"),sQuery(id+"F0.wireOp",EDGE,"E6.16.3"),sQuery(id+"F0.wireOp",EDGE,"E6.17.0"),sQuery(id+"F0.wireOp",EDGE,"E6.17.1"),sQuery(id+"F0.wireOp",EDGE,"E6.17.2"),sQuery(id+"F0.wireOp",EDGE,"E6.17.3"),sQuery(id+"F0.wireOp",EDGE,"E6.18.0"),sQuery(id+"F0.wireOp",EDGE,"E6.18.1"),sQuery(id+"F0.wireOp",EDGE,"E6.18.2"),sQuery(id+"F0.wireOp",EDGE,"E6.18.3"),sQuery(id+"F0.wireOp",EDGE,"E6.19.0"),sQuery(id+"F0.wireOp",EDGE,"E6.19.1"),sQuery(id+"F0.wireOp",EDGE,"E6.19.2"),sQuery(id+"F0.wireOp",EDGE,"E6.19.3"),sQuery(id+"F0.wireOp",EDGE,"E7.trimOffspring"),sQuery(id+"F0.wireOp",EDGE,"E8.trimOffspring"),sQuery(id+"F0.wireOp",EDGE,"E9.trimOffspring"),sQuery(id+"F0.wireOp",EDGE,"E10.trimOffspring"),sQuery(id+"F0.wireOp",EDGE,"E11.trimOffspring"),sQuery(id+"F0.wireOp",EDGE,"E12.trimOffspring"),sQuery(id+"F0.wireOp",EDGE,"E13.trimOffspring"),sQuery(id+"F0.wireOp",EDGE,"E14.trimOffspring"),sQuery(id+"F0.wireOp",EDGE,"E15.trimOffspring"),sQuery(id+"F0.wireOp",EDGE,"E16.trimOffspring"),sQuery(id+"F0.wireOp",EDGE,"E17.trimOffspring"),sQuery(id+"F0.wireOp",EDGE,"E18.trimOffspring"),sQuery(id+"F0.wireOp",EDGE,"E19.trimOffspring"),sQuery(id+"F0.wireOp",EDGE,"E20.trimOffspring"),sQuery(id+"F0.wireOp",EDGE,"E21.trimOffspring"),sQuery(id+"F0.wireOp",EDGE,"E22.trimOffspring"),sQuery(id+"F0.wireOp",EDGE,"E23.trimOffspring"),sQuery(id+"F0.wireOp",EDGE,"E24.trimOffspring"),sQuery(id+"F0.wireOp",EDGE,"E25.trimOffspring")])],"isStart":false});
            var sketch = newSketch(context, id + "F4", { "sketchPlane" : qUnion([Q0])});
            skCircle(sketch, "E26", {"center": v(0, 0) * mm, "radius": 90 * mm});
            skSolve(sketch);
        }
        {
            var Q0;
            Q0=makeQuery(id+"F4.imprint","IMPRINT",FACE,{"disambiguationData":[TD([[makeQuery(id+"F4.imprint","IMPRINT",EDGE,{"derivedFrom":sQuery(id+"F4.wireOp",EDGE,"E26")}),1.0]])]});
            extrude(context, id + "F5", {"entities" : qUnion([Q0]), "operationType" : NewBodyOperationType.REMOVE, "oppositeDirection" : true, "depth" : 5 * mm, "offsetDistance" : 25 * mm});
        }
        {
            var Q0;
            Q0=makeQuery(id+"F5.boolean.opBoolean","COPY",FACE,{"derivedFrom":makeQuery(id+"F5.opExtrude","CAP_FACE",FACE,{"disambiguationData":[OSD([sQuery(id+"F4.wireOp",EDGE,"E26")])],"isStart":false})});
            var sketch = newSketch(context, id + "F6", { "sketchPlane" : qUnion([Q0])});
            skCircle(sketch, "E27", {"center": v(0, 0) * mm, "radius": 30 * mm});
            skSolve(sketch);
        }
        {
            var Q0;
            Q0=makeQuery(id+"F6.imprint","IMPRINT",FACE,{"disambiguationData":[TD([[makeQuery(id+"F6.imprint","IMPRINT",EDGE,{"derivedFrom":sQuery(id+"F6.wireOp",EDGE,"E27")}),1.0]])]});
            extrude(context, id + "F7", {"entities" : qUnion([Q0]), "operationType" : NewBodyOperationType.ADD, "depth" : 30 * mm, "offsetDistance" : 25 * mm});
        }
        {
            var Q0;
            Q0=makeQuery(id+"F7.opExtrude","CAP_FACE",FACE,{"disambiguationData":[OSD([sQuery(id+"F6.wireOp",EDGE,"E27")])],"isStart":false});
            var sketch = newSketch(context, id + "F8", { "sketchPlane" : qUnion([Q0])});
            skCircle(sketch, "E28", {"center": v(0, 0) * mm, "radius": 15 * mm});
            skSolve(sketch);
        }
        {
            var Q0;
            Q0=makeQuery(id+"F8.imprint","IMPRINT",FACE,{"disambiguationData":[TD([[makeQuery(id+"F8.imprint","IMPRINT",EDGE,{"derivedFrom":sQuery(id+"F8.wireOp",EDGE,"E28")}),1.0]])]});
            extrude(context, id + "F9", {"entities" : qUnion([Q0]), "operationType" : NewBodyOperationType.REMOVE, "endBound" : BoundingType.THROUGH_ALL, "oppositeDirection" : true, "depth" : 25 * mm, "offsetDistance" : 25 * mm});
        }
        {
            var Q0;
            Q0=makeQuery(id+"F7.opExtrude","CAP_FACE",FACE,{"disambiguationData":[OSD([sQuery(id+"F6.wireOp",EDGE,"E27")])],"isStart":false});
            chamfer(context, id + "F10", {"entities" : qUnion([Q0]), "width" : 5 * mm, "tangentPropagation" : true});
        }
    });
